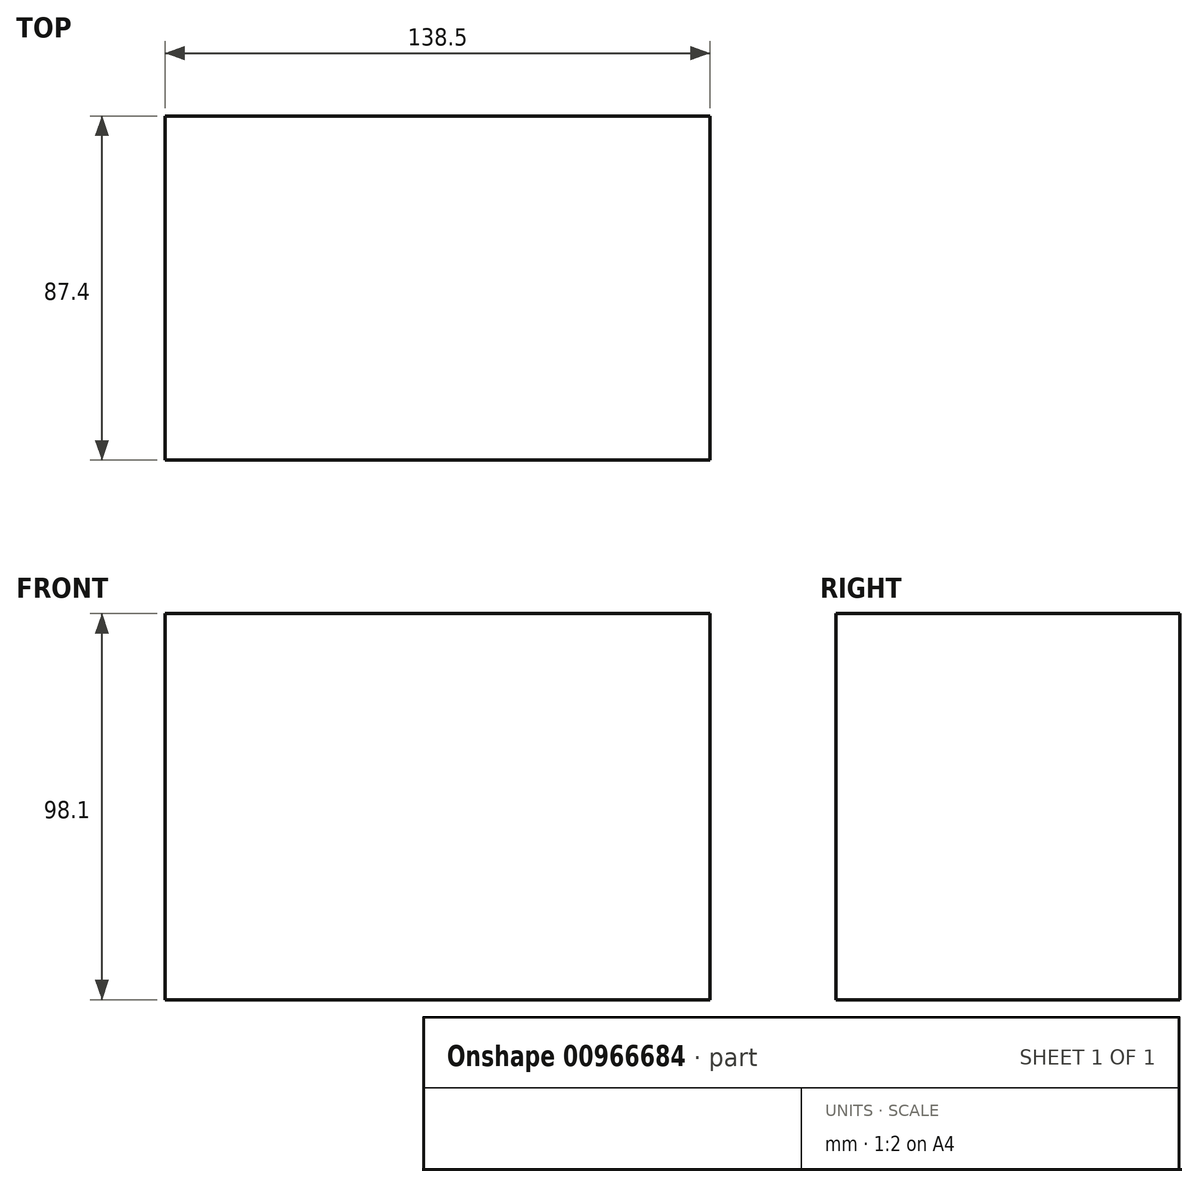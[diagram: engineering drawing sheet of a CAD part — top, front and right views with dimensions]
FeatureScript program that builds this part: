
annotation { "Feature Type Name" : "Feature", "Feature Type Description" : "" }
export const myFeature = defineFeature(function(context is Context, id is Id, definition is map)
    precondition{}
    {
        {
            var Q0;
            Q0=qCreatedBy(makeId("Top.planeOp"),FACE);
            var sketch = newSketch(context, id + "F0", { "sketchPlane" : qUnion([Q0])});
            skLineSegment(sketch, "E0.bottom", {"start": v(69.25, 43.7) * mm, "end": v(-69.25, 43.7) * mm});
            skLineSegment(sketch, "E0.top", {"start": v(69.25, -43.7) * mm, "end": v(-69.25, -43.7) * mm});
            skLineSegment(sketch, "E0.left", {"start": v(69.25, 43.7) * mm, "end": v(69.25, -43.7) * mm});
            skLineSegment(sketch, "E0.right", {"start": v(-69.25, 43.7) * mm, "end": v(-69.25, -43.7) * mm});
            skPoint(sketch, "E0.middle", {"position": v(0, 0) * mm});
            skSolve(sketch);
        }
        {
            var Q0;
            Q0=makeQuery(id+"F0.imprint","IMPRINT",FACE,{"disambiguationData":[TD([[makeQuery(id+"F0.imprint","IMPRINT",EDGE,{"derivedFrom":sQuery(id+"F0.wireOp",EDGE,"E0.bottom")}),1.0]])]});
            extrude(context, id + "F1", {"entities" : qUnion([Q0]), "depth" : 98.1 * mm, "offsetDistance" : 25 * mm});
        }
    });
